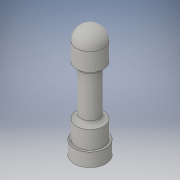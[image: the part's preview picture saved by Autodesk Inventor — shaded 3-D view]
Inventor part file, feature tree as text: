
AUTODESK INVENTOR PART (.ipt)
format: ipt  version: 2016 (Build 200138000, 138)  size: 141,824 bytes
history: native  units: in
note: dims shown in document units (in); Inventor stores cm internally (conversion verified against a paired STEP export)
features: revolve x1, fillet x1, sketch x1
ambient origin geometry x8: Origin, YZ Plane, XZ Plane, XY Plane, X Axis, Y Axis, Z Axis, Center Point
bodies: Solid1 (feature_tree)
feature tree (3):
  revolve  "Revolution1"  [1 undecoded]
  fillet  "Fillet1"  Radius=0.0197in
  sketch  "Sketch1"  dims[d0=0.1378in d1=0.1181in d2=0.0197in d3=0.1575in d4=0.0394in d5=0.4331in d6=0.0394in d7=0.1575in d8=0.2362in d9=0.1181in d10=90.0deg d11=0.0394in d12=0.1575in]
note: 1 required parameter value undecoded (feature->parameter linkage not recoverable at this tier; creation-order binding heuristic only, values carry confidence <= 0.55)
